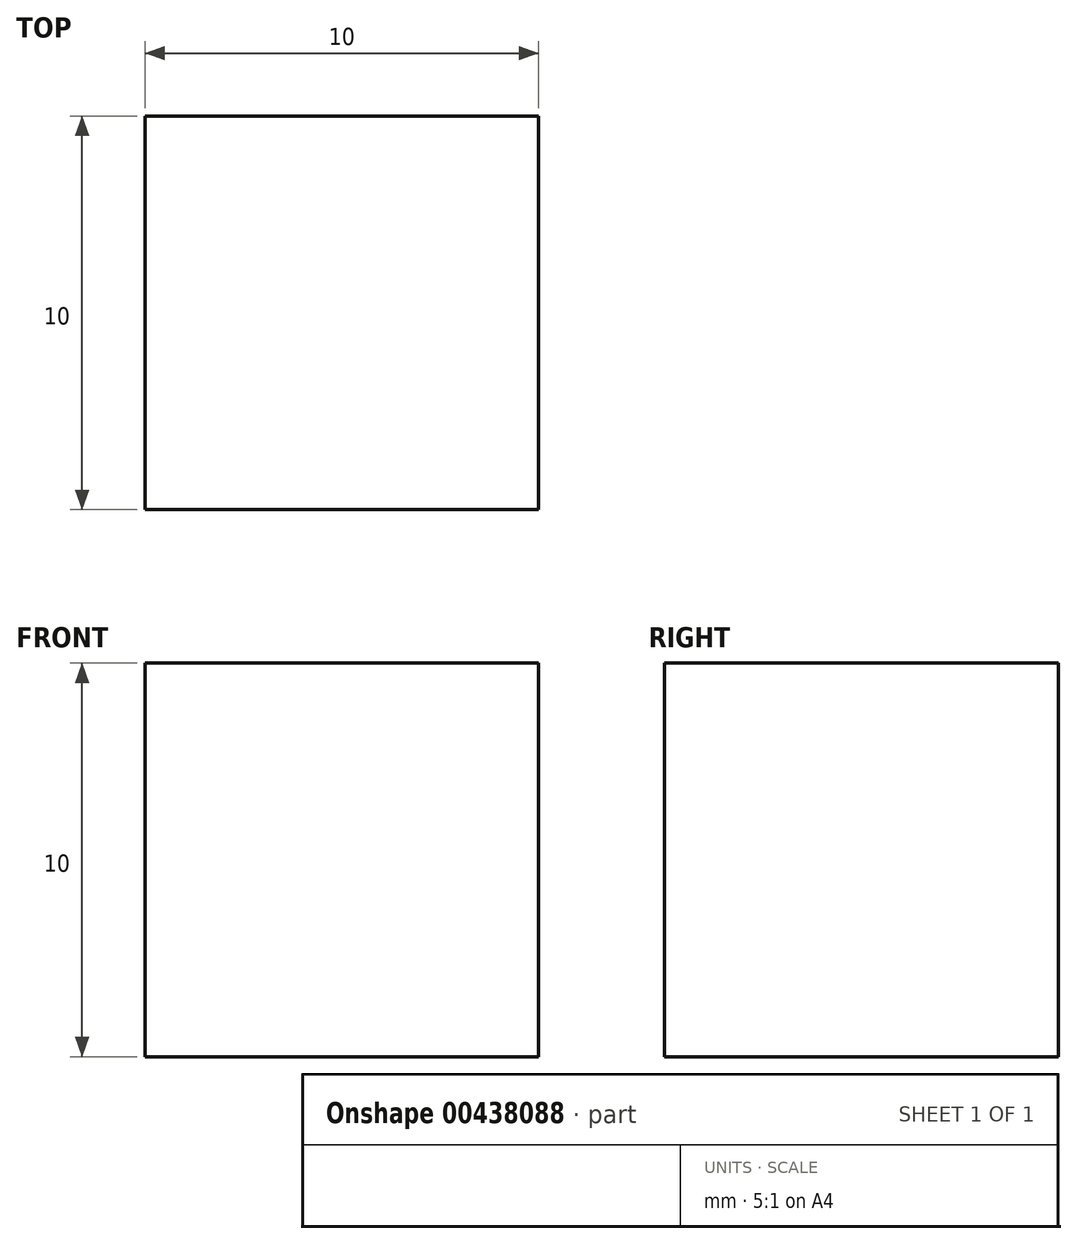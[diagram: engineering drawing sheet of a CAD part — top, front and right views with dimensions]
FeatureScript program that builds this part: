
annotation { "Feature Type Name" : "Feature", "Feature Type Description" : "" }
export const myFeature = defineFeature(function(context is Context, id is Id, definition is map)
    precondition{}
    {
        {
            var Q0;
            Q0=qCreatedBy(makeId("Top.planeOp"),FACE);
            var sketch = newSketch(context, id + "F0", { "sketchPlane" : qUnion([Q0])});
            skLineSegment(sketch, "E0.rect.bottom", {"start": v(-5, 5) * mm, "end": v(5, 5) * mm});
            skLineSegment(sketch, "E0.rect.top", {"start": v(-5, -5) * mm, "end": v(5, -5) * mm});
            skLineSegment(sketch, "E0.rect.left", {"start": v(-5, 5) * mm, "end": v(-5, -5) * mm});
            skLineSegment(sketch, "E0.rect.right", {"start": v(5, 5) * mm, "end": v(5, -5) * mm});
            skPoint(sketch, "E0.rect.middle", {"position": v(0, 0) * mm});
            skSolve(sketch);
        }
        {
            var Q0;
            Q0=qSketchRegion(id+"F0",true);
            extrude(context, id + "F1", {"entities" : qUnion([Q0]), "depth" : 10 * mm});
        }
    });
